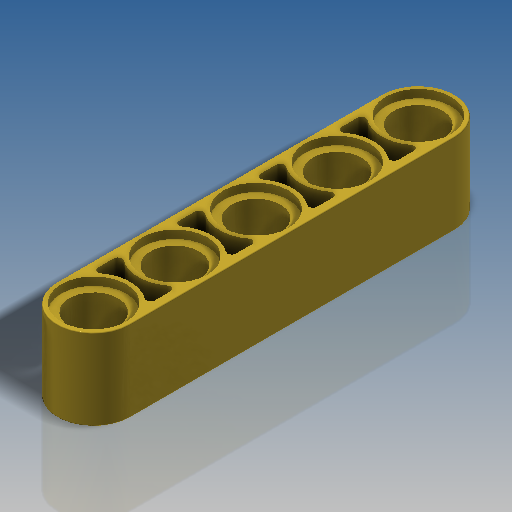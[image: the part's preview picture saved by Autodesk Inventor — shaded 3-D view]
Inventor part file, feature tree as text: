
AUTODESK INVENTOR PART (.ipt)
format: ipt  version: 2018.3 (Build 223284000, 284)  size: 355,328 bytes
history: native  units: mm
features: extrude x3, sketch x2, mirror x1, fillet x1
ambient origin geometry x8: Origin, YZ Plane, XZ Plane, XY Plane, X Axis, Y Axis, Z Axis, Center Point
bodies: Solid1 (feature_tree)
feature tree (7):
  extrude  "Extrusion1"  Depth=6.4mm
  sketch  "Sketch6"  dims[d14=8.0mm d15=0.0mm d32=7.2mm d34=8.0mm d36=0.8mm d41=0.8mm d42=0.0mm d43=3.1mm d44=0.0mm d46=0.4mm d47=0.1mm]
  extrude  "Extrusion7"  Depth=7.2mm
  extrude  "Extrusion8"  Depth=8.0mm
  mirror  "Mirror1"
  fillet  "Fillet1"  Radius=0.8mm
  sketch  "Sketch1"  dims[d8=4.8mm d9=6.4mm]
